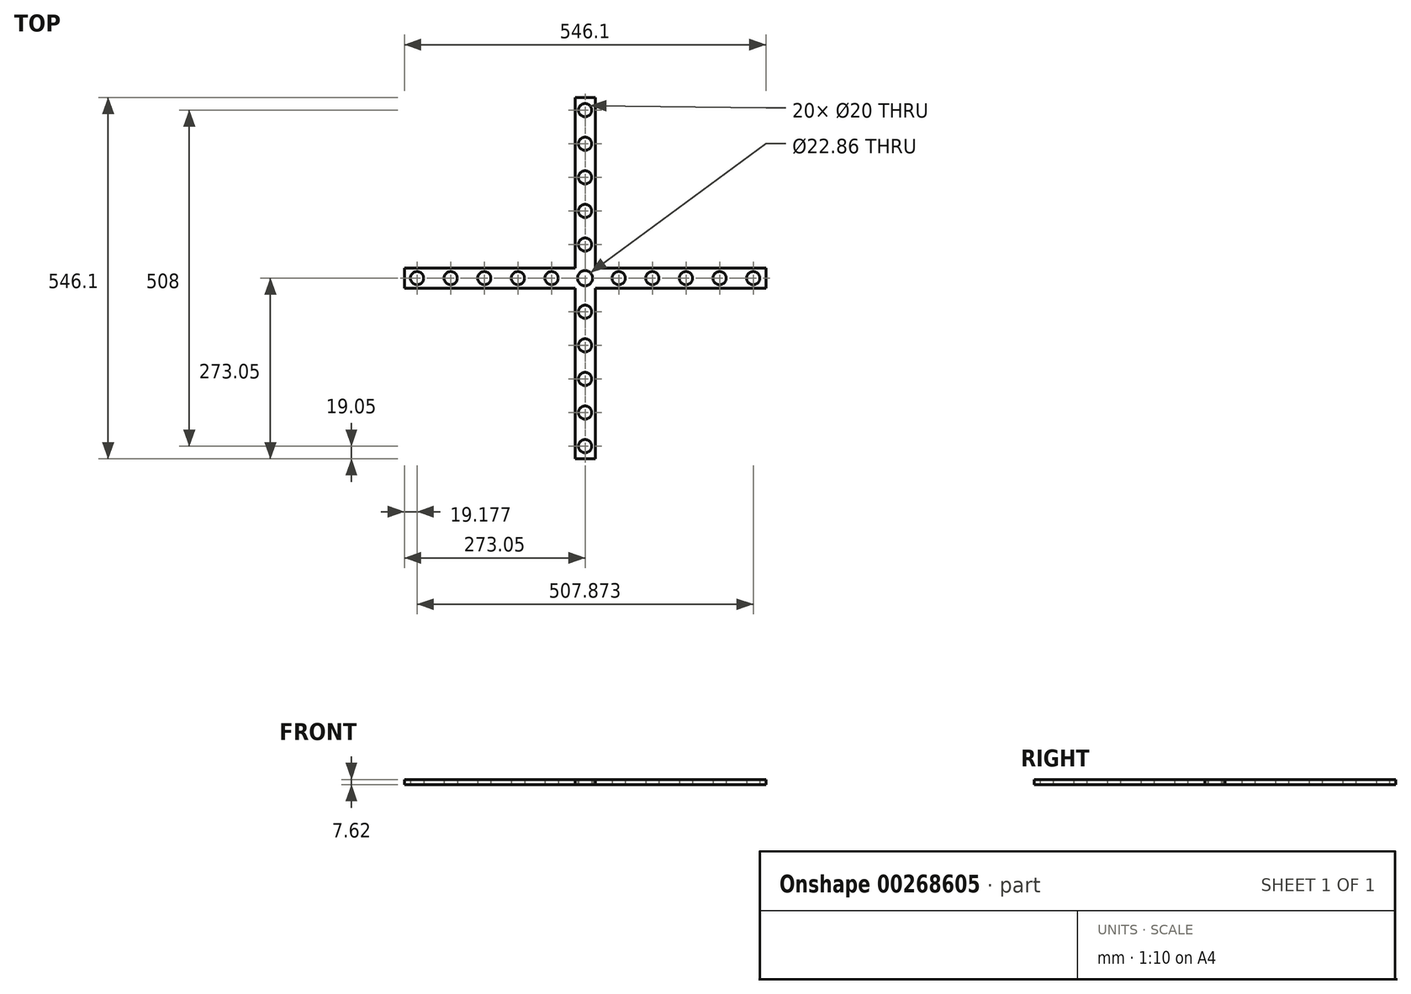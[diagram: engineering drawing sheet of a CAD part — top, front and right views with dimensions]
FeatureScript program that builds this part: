
annotation { "Feature Type Name" : "Feature", "Feature Type Description" : "" }
export const myFeature = defineFeature(function(context is Context, id is Id, definition is map)
    precondition{}
    {
        {
            var Q0;
            Q0=qCreatedBy(makeId("Top.planeOp"),FACE);
            var sketch = newSketch(context, id + "F0", { "sketchPlane" : qUnion([Q0])});
            skPoint(sketch, "E0.middle", {"position": v(0, 0) * mm});
            skCircle(sketch, "E1", {"center": v(0, 0) * mm, "radius": 11.43 * mm});
            skCircle(sketch, "E2", {"center": v(-50.67, 0) * mm, "radius": 10 * mm});
            skCircle(sketch, "E3", {"center": v(50.8, 0) * mm, "radius": 10 * mm});
            skCircle(sketch, "E4.1.0.0", {"center": v(-101.47, 0) * mm, "radius": 10 * mm});
            skCircle(sketch, "E4.2.0.0", {"center": v(-152.27, 0) * mm, "radius": 10 * mm});
            skCircle(sketch, "E4.3.0.0", {"center": v(-203.07, 0) * mm, "radius": 10 * mm});
            skCircle(sketch, "E4.4.0.0", {"center": v(-253.87, 0) * mm, "radius": 10 * mm});
            skCircle(sketch, "E5.1.0.0", {"center": v(101.6, 0) * mm, "radius": 10 * mm});
            skCircle(sketch, "E5.2.0.0", {"center": v(152.4, 0) * mm, "radius": 10 * mm});
            skCircle(sketch, "E5.3.0.0", {"center": v(203.2, 0) * mm, "radius": 10 * mm});
            skCircle(sketch, "E5.4.0.0", {"center": v(254, 0) * mm, "radius": 10 * mm});
            skLineSegment(sketch, "E6.bottom", {"start": v(-273.05, 15.24) * mm, "end": v(273.05, 15.24) * mm});
            skLineSegment(sketch, "E6.top", {"start": v(-273.05, -15.24) * mm, "end": v(273.05, -15.24) * mm});
            skLineSegment(sketch, "E6.left", {"start": v(-273.05, 15.24) * mm, "end": v(-273.05, -15.24) * mm});
            skLineSegment(sketch, "E6.right", {"start": v(273.05, 15.24) * mm, "end": v(273.05, -15.24) * mm});
            skLineSegment(sketch, "E7.bottom", {"start": v(-15.24, 273.05) * mm, "end": v(15.24, 273.05) * mm});
            skLineSegment(sketch, "E7.top", {"start": v(-15.24, -273.05) * mm, "end": v(15.24, -273.05) * mm});
            skLineSegment(sketch, "E7.left", {"start": v(-15.24, 273.05) * mm, "end": v(-15.24, -273.05) * mm});
            skLineSegment(sketch, "E7.right", {"start": v(15.24, 273.05) * mm, "end": v(15.24, -273.05) * mm});
            skCircle(sketch, "E8", {"center": v(0, 50.8) * mm, "radius": 10 * mm});
            skCircle(sketch, "E9", {"center": v(0, -50.8) * mm, "radius": 10 * mm});
            skCircle(sketch, "E10.0.1.0", {"center": v(0, -101.6) * mm, "radius": 10 * mm});
            skCircle(sketch, "E10.0.2.0", {"center": v(0, -152.4) * mm, "radius": 10 * mm});
            skCircle(sketch, "E10.0.3.0", {"center": v(0, -203.2) * mm, "radius": 10 * mm});
            skCircle(sketch, "E10.0.4.0", {"center": v(0, -254) * mm, "radius": 10 * mm});
            skCircle(sketch, "E11.0.1.0", {"center": v(0, 101.6) * mm, "radius": 10 * mm});
            skCircle(sketch, "E11.0.2.0", {"center": v(0, 152.4) * mm, "radius": 10 * mm});
            skCircle(sketch, "E11.0.3.0", {"center": v(0, 203.2) * mm, "radius": 10 * mm});
            skCircle(sketch, "E11.0.4.0", {"center": v(0, 254) * mm, "radius": 10 * mm});
            skSolve(sketch);
        }
        {
            var Q0;
            Q0=makeQuery(id+"F0.imprint","IMPRINT",FACE,{"disambiguationData":[TD([[makeQuery(id+"F0.imprint","IMPRINT",EDGE,{"derivedFrom":sQuery(id+"F0.wireOp",EDGE,"E2")}),-1.0]])]});
            var Q1;
            {var subQ1=sQuery(id+"F0.wireOp",EDGE,"E7.top");Q1=makeQuery(id+"F0.imprint","IMPRINT",FACE,{"disambiguationData":[TD([[makeQuery(id+"F0.imprint","IMPRINT",EDGE,{"derivedFrom":subQ1}),1.0]])]});}
            var Q2;
            Q2=makeQuery(id+"F0.imprint","IMPRINT",FACE,{"disambiguationData":[TD([[makeQuery(id+"F0.imprint","IMPRINT",EDGE,{"derivedFrom":sQuery(id+"F0.wireOp",EDGE,"E3")}),-1.0]])]});
            var Q3;
            {var subQ1=sQuery(id+"F0.wireOp",EDGE,"E7.bottom");Q3=makeQuery(id+"F0.imprint","IMPRINT",FACE,{"disambiguationData":[TD([[makeQuery(id+"F0.imprint","IMPRINT",EDGE,{"derivedFrom":subQ1}),-1.0]])]});}
            var Q4;
            Q4=makeQuery(id+"F0.imprint","IMPRINT",FACE,{"disambiguationData":[TD([[makeQuery(id+"F0.imprint","IMPRINT",EDGE,{"derivedFrom":sQuery(id+"F0.wireOp",EDGE,"E1")}),-1.0]])]});
            extrude(context, id + "F1", {"entities" : qUnion([Q0, Q1, Q2, Q3, Q4]), "depth" : 7.62 * mm, "offsetDistance" : 25.4 * mm});
        }
    });
